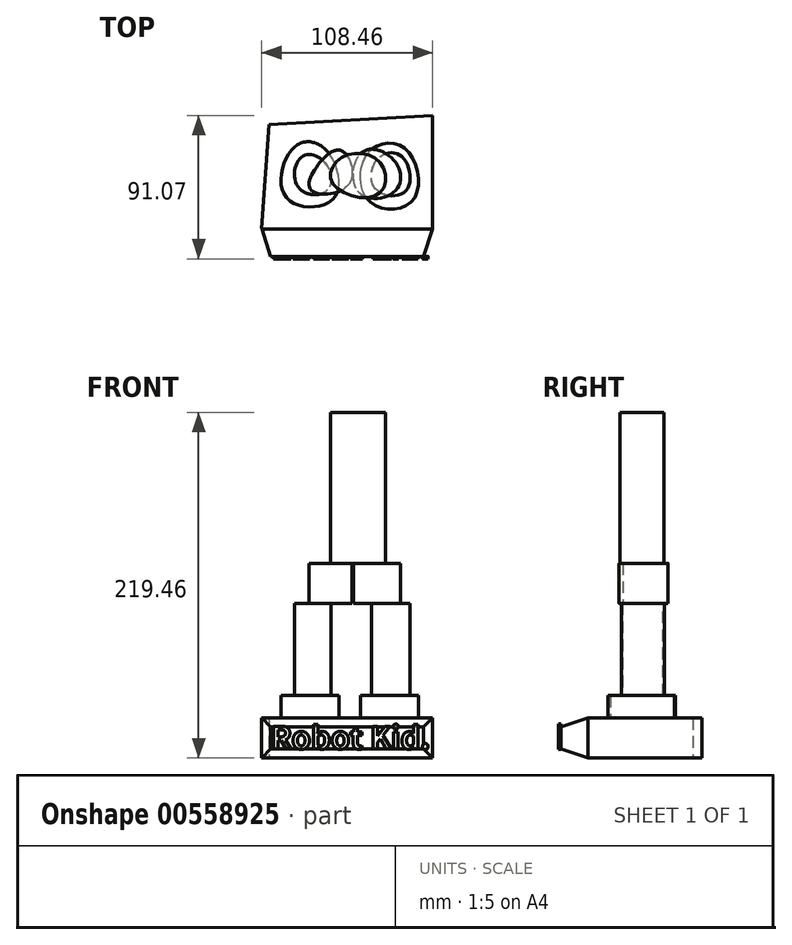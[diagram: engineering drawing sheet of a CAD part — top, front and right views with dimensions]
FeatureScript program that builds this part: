
annotation { "Feature Type Name" : "Feature", "Feature Type Description" : "" }
export const myFeature = defineFeature(function(context is Context, id is Id, definition is map)
    precondition{}
    {
        {
            var Q0;
            Q0=qCreatedBy(makeId("Top.planeOp"),FACE);
            var sketch = newSketch(context, id + "F0", { "sketchPlane" : qUnion([Q0])});
            skLineSegment(sketch, "E0", {"start": v(-46.36, 37.86) * mm, "end": v(-52.13, -46) * mm});
            skLineSegment(sketch, "E1", {"start": v(-52.13, -46) * mm, "end": v(57.55, -46) * mm});
            skLineSegment(sketch, "E2", {"start": v(57.55, -46) * mm, "end": v(57.55, 43.55) * mm});
            skLineSegment(sketch, "E3", {"start": v(57.55, 43.55) * mm, "end": v(-46.36, 37.86) * mm});
            skSolve(sketch);
        }
        {
            var Q0;
            Q0 = qSketchRegion(id + "F0", true);
            extrude(context, id + "F1", {"entities" : qUnion([Q0]), "depth" : 25.4 * mm, "offsetDistance" : 25.4 * mm});
        }
        {
            var Q0;
            Q0=makeQuery(id+"F1.opExtrude","SWEPT_FACE",FACE,{"disambiguationData":[OSD([sQuery(id+"F0.wireOp",EDGE,"E1")])]});
            chamfer(context, id + "F2", {"entities" : qUnion([Q0]), "chamferType" : ChamferType.TWO_OFFSETS, "width1" : 17.78 * mm, "oppositeDirection" : true, "width2" : 6.86 * mm, "tangentPropagation" : true});
        }
        {
            var Q0;
            Q0=makeQuery(id+"F1.opExtrude","SWEPT_FACE",FACE,{"disambiguationData":[OSD([sQuery(id+"F0.wireOp",EDGE,"E1")])]});
            var sketch = newSketch(context, id + "F3", { "sketchPlane" : qUnion([Q0])});
            skText(sketch, "E4", { "text": "Robot Kid. ", "fontName": "NotoSansCJKkr-Bold.otf"});
            const initialGuessF3  = {"E4": [-0.04527, 0.00565, 1, 0, 0.0141]};
            skSetInitialGuess(sketch, initialGuessF3);
            skSolve(sketch);
        }
        {
            var Q0;
            Q0 = qSketchRegion(id + "F3", true);
            extrude(context, id + "F4", {"entities" : qUnion([Q0]), "operationType" : NewBodyOperationType.ADD, "depth" : 1.52 * mm, "offsetDistance" : 25.4 * mm});
        }
        {
            var Q0;
            Q0=makeQuery(id+"F1.opExtrude","CAP_FACE",FACE,{"disambiguationData":[OSD([sQuery(id+"F0.wireOp",EDGE,"E0"),sQuery(id+"F0.wireOp",EDGE,"E1"),sQuery(id+"F0.wireOp",EDGE,"E2"),sQuery(id+"F0.wireOp",EDGE,"E3")])],"isStart":false});
            var sketch = newSketch(context, id + "F5", { "sketchPlane" : qUnion([Q0])});
            skFitSpline(sketch, "E5", {"points": [v(-29.8, 23.78) * mm, v(-35.39, -8.4) * mm, v(-5.18, -8.95) * mm, v(-9.65, 21.26) * mm, v(-29.8, 23.78) * mm]});
            skFitSpline(sketch, "E6", {"points": [v(16.37, 19.3) * mm, v(39.87, 22.66) * mm, v(45.46, -9.8) * mm, v(17.76, -11.2) * mm, v(16.37, 19.3) * mm]});
            skSolve(sketch);
        }
        {
            var Q0;
            Q0 = qSketchRegion(id + "F5", true);
            extrude(context, id + "F6", {"entities" : qUnion([Q0]), "operationType" : NewBodyOperationType.ADD, "depth" : 14.22 * mm, "offsetDistance" : 25.4 * mm});
        }
        {
            var Q0;
            Q0=makeQuery(id+"F6.opExtrude","CAP_FACE",FACE,{"disambiguationData":[OSD([sQuery(id+"F5.wireOp",EDGE,"E5")])],"isStart":false});
            var sketch = newSketch(context, id + "F7", { "sketchPlane" : qUnion([Q0])});
            skFitSpline(sketch, "E7", {"points": [v(-26.82, -2.93) * mm, v(-26.33, 16.68) * mm, v(-11.8, 14.78) * mm, v(-8.88, -3.6) * mm, v(-26.82, -2.93) * mm]});
            skFitSpline(sketch, "E8", {"points": [v(21.45, -3.2) * mm, v(23.06, 16.37) * mm, v(38.26, 17.28) * mm, v(40.77, -4.2) * mm, v(21.45, -3.2) * mm]});
            skSolve(sketch);
        }
        {
            var Q0;
            Q0 = qSketchRegion(id + "F7", true);
            extrude(context, id + "F8", {"entities" : qUnion([Q0]), "operationType" : NewBodyOperationType.ADD, "depth" : 58.67 * mm, "offsetDistance" : 25.4 * mm});
        }
        {
            var Q0;
            Q0=makeQuery(id+"F8.opExtrude","CAP_FACE",FACE,{"disambiguationData":[OSD([sQuery(id+"F7.wireOp",EDGE,"E8")])],"isStart":false});
            var sketch = newSketch(context, id + "F9", { "sketchPlane" : qUnion([Q0])});
            skFitSpline(sketch, "E9", {"points": [v(-15.57, 11.55) * mm, v(0, 21.1) * mm, v(4.54, 0) * mm, v(-19.15, -4.15) * mm, v(-15.57, 11.55) * mm]});
            skFitSpline(sketch, "E10", {"points": [v(33.87, 14.11) * mm, v(33.77, -4.4) * mm, v(10.83, -5.34) * mm, v(13.21, 20.49) * mm, v(33.87, 14.11) * mm]});
            skSolve(sketch);
        }
        {
            var Q0;
            Q0 = qSketchRegion(id + "F9", true);
            extrude(context, id + "F10", {"entities" : qUnion([Q0]), "operationType" : NewBodyOperationType.ADD, "depth" : 25.4 * mm, "offsetDistance" : 25.4 * mm});
        }
        {
            var Q0;
            Q0=makeQuery(id+"F10.opExtrude","CAP_FACE",FACE,{"disambiguationData":[OSD([sQuery(id+"F9.wireOp",EDGE,"E10")])],"isStart":false});
            var sketch = newSketch(context, id + "F11", { "sketchPlane" : qUnion([Q0])});
            skFitSpline(sketch, "E11", {"points": [v(24.33, 13.72) * mm, v(0, 16.94) * mm, v(-5.55, 0) * mm, v(23.1, -6.41) * mm, v(24.33, 13.72) * mm]});
            skSolve(sketch);
        }
        {
            var Q0;
            Q0 = qSketchRegion(id + "F11", true);
            extrude(context, id + "F12", {"entities" : qUnion([Q0]), "operationType" : NewBodyOperationType.ADD, "depth" : 95.76 * mm, "offsetDistance" : 25.4 * mm});
        }
    });
